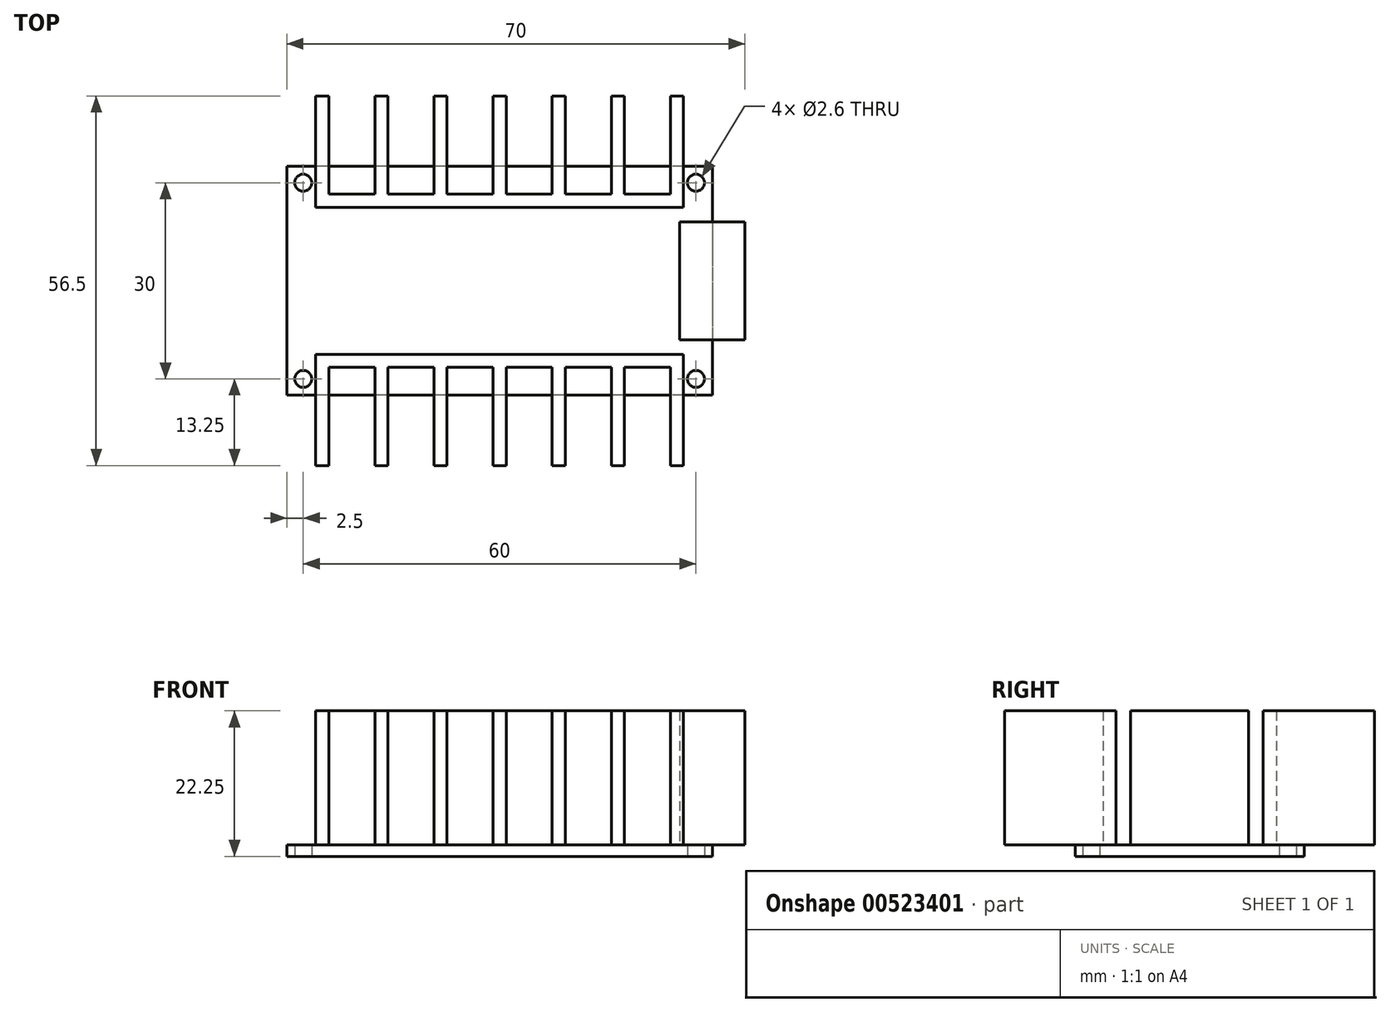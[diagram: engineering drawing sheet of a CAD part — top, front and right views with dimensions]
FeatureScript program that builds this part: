
annotation { "Feature Type Name" : "Feature", "Feature Type Description" : "" }
export const myFeature = defineFeature(function(context is Context, id is Id, definition is map)
    precondition{}
    {
        {
            var Q0;
            Q0=qCreatedBy(makeId("Top.planeOp"),FACE);
            var sketch = newSketch(context, id + "F0", { "sketchPlane" : qUnion([Q0])});
            skLineSegment(sketch, "E0.bottom", {"start": v(32.5, 17.5) * mm, "end": v(-32.5, 17.5) * mm});
            skLineSegment(sketch, "E0.top", {"start": v(32.5, -17.5) * mm, "end": v(-32.5, -17.5) * mm});
            skLineSegment(sketch, "E0.left", {"start": v(32.5, 17.5) * mm, "end": v(32.5, -17.5) * mm});
            skLineSegment(sketch, "E0.right", {"start": v(-32.5, 17.5) * mm, "end": v(-32.5, -17.5) * mm});
            skPoint(sketch, "E0.middle", {"position": v(0, 0) * mm});
            skCircle(sketch, "E1", {"center": v(-30, 15) * mm, "radius": 1.3 * mm});
            skCircle(sketch, "E2", {"center": v(30, 15) * mm, "radius": 1.3 * mm});
            skCircle(sketch, "E3", {"center": v(-30, -15) * mm, "radius": 1.3 * mm});
            skCircle(sketch, "E4", {"center": v(30, -15) * mm, "radius": 1.3 * mm});
            skLineSegment(sketch, "E5", {"start": v(-30, 15) * mm, "end": v(30, 15) * mm, "construction": true});
            skLineSegment(sketch, "E6", {"start": v(30, -15) * mm, "end": v(-30, -15) * mm, "construction": true});
            skLineSegment(sketch, "E7", {"start": v(-30, 15) * mm, "end": v(-30, -15) * mm, "construction": true});
            skLineSegment(sketch, "E8", {"start": v(30, 15) * mm, "end": v(30, -15) * mm, "construction": true});
            skLineSegment(sketch, "E9", {"start": v(0, -15) * mm, "end": v(0, -17.5) * mm, "construction": true});
            skLineSegment(sketch, "E10", {"start": v(0, 17.5) * mm, "end": v(0, 15) * mm, "construction": true});
            skLineSegment(sketch, "E11", {"start": v(-32.5, 0) * mm, "end": v(-30, 0) * mm, "construction": true});
            skLineSegment(sketch, "E12", {"start": v(30, 0) * mm, "end": v(32.5, 0) * mm, "construction": true});
            skSolve(sketch);
        }
        {
            var Q0;
            Q0 = qSketchRegion(id + "F0", true);
            extrude(context, id + "F1", {"entities" : qUnion([Q0]), "depth" : 1.75 * mm, "offsetDistance" : 25 * mm});
        }
        {
            var Q0;
            Q0=makeQuery(id+"F1.opExtrude","CAP_FACE",FACE,{"disambiguationData":[OSD([sQuery(id+"F0.wireOp",EDGE,"E0.bottom"),sQuery(id+"F0.wireOp",EDGE,"E0.top"),sQuery(id+"F0.wireOp",EDGE,"E0.left"),sQuery(id+"F0.wireOp",EDGE,"E0.right"),sQuery(id+"F0.wireOp",EDGE,"E1"),sQuery(id+"F0.wireOp",EDGE,"E2"),sQuery(id+"F0.wireOp",EDGE,"E3"),sQuery(id+"F0.wireOp",EDGE,"E4")])],"isStart":false});
            var sketch = newSketch(context, id + "F2", { "sketchPlane" : qUnion([Q0])});
            skLineSegment(sketch, "E13", {"start": v(-12.02, 0) * mm, "end": v(12.3, 0) * mm, "construction": true});
            skLineSegment(sketch, "E14.bottom", {"start": v(-28.1, 28.25) * mm, "end": v(-26.1, 28.25) * mm});
            skLineSegment(sketch, "E14.top", {"start": v(-28.1, 13.25) * mm, "end": v(-26.1, 13.25) * mm});
            skLineSegment(sketch, "E14.left", {"start": v(-28.1, 28.25) * mm, "end": v(-28.1, 13.25) * mm});
            skLineSegment(sketch, "E14.right", {"start": v(-26.1, 28.25) * mm, "end": v(-26.1, 13.25) * mm});
            skLineSegment(sketch, "E15.bottom", {"start": v(-10.03, 28.25) * mm, "end": v(-8.03, 28.25) * mm});
            skLineSegment(sketch, "E15.top", {"start": v(-10.03, 13.25) * mm, "end": v(-8.03, 13.25) * mm});
            skLineSegment(sketch, "E15.left", {"start": v(-10.03, 28.25) * mm, "end": v(-10.03, 13.25) * mm});
            skLineSegment(sketch, "E15.right", {"start": v(-8.03, 28.25) * mm, "end": v(-8.03, 13.25) * mm});
            skLineSegment(sketch, "E16.bottom", {"start": v(17.07, 28.25) * mm, "end": v(19.07, 28.25) * mm});
            skLineSegment(sketch, "E16.top", {"start": v(17.07, 13.25) * mm, "end": v(19.07, 13.25) * mm});
            skLineSegment(sketch, "E16.left", {"start": v(17.07, 28.25) * mm, "end": v(17.07, 13.25) * mm});
            skLineSegment(sketch, "E16.right", {"start": v(19.07, 28.25) * mm, "end": v(19.07, 13.25) * mm});
            skLineSegment(sketch, "E17.bottom", {"start": v(1, 28.25) * mm, "end": v(-1, 28.25) * mm});
            skLineSegment(sketch, "E17.top", {"start": v(1, 13.25) * mm, "end": v(-1, 13.25) * mm});
            skLineSegment(sketch, "E17.left", {"start": v(1, 28.25) * mm, "end": v(1, 13.25) * mm});
            skLineSegment(sketch, "E17.right", {"start": v(-1, 28.25) * mm, "end": v(-1, 13.25) * mm});
            skLineSegment(sketch, "E18.bottom", {"start": v(-19.07, 13.25) * mm, "end": v(-17.07, 13.25) * mm});
            skLineSegment(sketch, "E18.top", {"start": v(-19.07, 28.25) * mm, "end": v(-17.07, 28.25) * mm});
            skLineSegment(sketch, "E18.left", {"start": v(-19.07, 13.25) * mm, "end": v(-19.07, 28.25) * mm});
            skLineSegment(sketch, "E18.right", {"start": v(-17.07, 13.25) * mm, "end": v(-17.07, 28.25) * mm});
            skLineSegment(sketch, "E19.bottom", {"start": v(8.03, 13.25) * mm, "end": v(10.03, 13.25) * mm});
            skLineSegment(sketch, "E19.top", {"start": v(8.03, 28.25) * mm, "end": v(10.03, 28.25) * mm});
            skLineSegment(sketch, "E19.left", {"start": v(8.03, 13.25) * mm, "end": v(8.03, 28.25) * mm});
            skLineSegment(sketch, "E19.right", {"start": v(10.03, 13.25) * mm, "end": v(10.03, 28.25) * mm});
            skLineSegment(sketch, "E20.bottom", {"start": v(26.1, 28.25) * mm, "end": v(28.1, 28.25) * mm});
            skLineSegment(sketch, "E20.top", {"start": v(26.1, 13.25) * mm, "end": v(28.1, 13.25) * mm});
            skLineSegment(sketch, "E20.left", {"start": v(26.1, 28.25) * mm, "end": v(26.1, 13.25) * mm});
            skLineSegment(sketch, "E20.right", {"start": v(28.1, 28.25) * mm, "end": v(28.1, 13.25) * mm});
            skLineSegment(sketch, "E21.bottom", {"start": v(-28.1, 13.25) * mm, "end": v(28.1, 13.25) * mm});
            skLineSegment(sketch, "E21.top", {"start": v(-28.1, 11.25) * mm, "end": v(28.1, 11.25) * mm});
            skLineSegment(sketch, "E21.left", {"start": v(-28.1, 13.25) * mm, "end": v(-28.1, 11.25) * mm});
            skLineSegment(sketch, "E21.right", {"start": v(28.1, 13.25) * mm, "end": v(28.1, 11.25) * mm});
            skPoint(sketch, "E22", {"position": v(0, 11.25) * mm});
            skLineSegment(sketch, "E23", {"start": v(-26.1, 28.25) * mm, "end": v(-19.07, 28.25) * mm, "construction": true});
            skLineSegment(sketch, "E24", {"start": v(-17.07, 28.25) * mm, "end": v(-10.03, 28.25) * mm, "construction": true});
            skLineSegment(sketch, "E25", {"start": v(-8.03, 28.25) * mm, "end": v(-1, 28.25) * mm, "construction": true});
            skLineSegment(sketch, "E26", {"start": v(1, 28.25) * mm, "end": v(8.03, 28.25) * mm, "construction": true});
            skLineSegment(sketch, "E27", {"start": v(10.03, 28.25) * mm, "end": v(17.07, 28.25) * mm, "construction": true});
            skLineSegment(sketch, "E28", {"start": v(19.07, 28.25) * mm, "end": v(26.1, 28.25) * mm, "construction": true});
            skLineSegment(sketch, "E29.MirrorCS", {"start": v(-10.03, -28.25) * mm, "end": v(-10.03, -13.25) * mm});
            skLineSegment(sketch, "E30.MirrorCS", {"start": v(-19.07, -13.25) * mm, "end": v(-19.07, -28.25) * mm});
            skLineSegment(sketch, "E31.MirrorCS", {"start": v(28.1, -13.25) * mm, "end": v(28.1, -11.25) * mm});
            skLineSegment(sketch, "E32.MirrorCS", {"start": v(10.03, -28.25) * mm, "end": v(17.07, -28.25) * mm, "construction": true});
            skLineSegment(sketch, "E33.MirrorCS", {"start": v(-8.03, -28.25) * mm, "end": v(-1, -28.25) * mm, "construction": true});
            skLineSegment(sketch, "E34.MirrorCS", {"start": v(-1, -28.25) * mm, "end": v(-1, -13.25) * mm});
            skLineSegment(sketch, "E35.MirrorCS", {"start": v(26.1, -28.25) * mm, "end": v(26.1, -13.25) * mm});
            skLineSegment(sketch, "E36.MirrorCS", {"start": v(-26.1, -28.25) * mm, "end": v(-26.1, -13.25) * mm});
            skLineSegment(sketch, "E37.MirrorCS", {"start": v(1, -13.25) * mm, "end": v(-1, -13.25) * mm});
            skLineSegment(sketch, "E38.MirrorCS", {"start": v(17.07, -28.25) * mm, "end": v(19.07, -28.25) * mm});
            skLineSegment(sketch, "E39.MirrorCS", {"start": v(-17.07, -13.25) * mm, "end": v(-17.07, -28.25) * mm});
            skLineSegment(sketch, "E40.MirrorCS", {"start": v(-26.1, -28.25) * mm, "end": v(-19.07, -28.25) * mm, "construction": true});
            skLineSegment(sketch, "E41.MirrorCS", {"start": v(-10.03, -13.25) * mm, "end": v(-8.03, -13.25) * mm});
            skLineSegment(sketch, "E42.MirrorCS", {"start": v(-28.1, -13.25) * mm, "end": v(-26.1, -13.25) * mm});
            skLineSegment(sketch, "E43.MirrorCS", {"start": v(26.1, -13.25) * mm, "end": v(28.1, -13.25) * mm});
            skLineSegment(sketch, "E44.MirrorCS", {"start": v(-28.1, -11.25) * mm, "end": v(28.1, -11.25) * mm});
            skLineSegment(sketch, "E45.MirrorCS", {"start": v(-28.1, -28.25) * mm, "end": v(-26.1, -28.25) * mm});
            skLineSegment(sketch, "E46.MirrorCS", {"start": v(1, -28.25) * mm, "end": v(1, -13.25) * mm});
            skLineSegment(sketch, "E47.MirrorCS", {"start": v(8.03, -13.25) * mm, "end": v(10.03, -13.25) * mm});
            skLineSegment(sketch, "E48.MirrorCS", {"start": v(17.07, -13.25) * mm, "end": v(19.07, -13.25) * mm});
            skLineSegment(sketch, "E49.MirrorCS", {"start": v(-8.03, -28.25) * mm, "end": v(-8.03, -13.25) * mm});
            skLineSegment(sketch, "E50.MirrorCS", {"start": v(-28.1, -13.25) * mm, "end": v(28.1, -13.25) * mm});
            skLineSegment(sketch, "E51.MirrorCS", {"start": v(1, -28.25) * mm, "end": v(8.03, -28.25) * mm, "construction": true});
            skLineSegment(sketch, "E52.MirrorCS", {"start": v(8.03, -28.25) * mm, "end": v(10.03, -28.25) * mm});
            skLineSegment(sketch, "E53.MirrorCS", {"start": v(-28.1, -13.25) * mm, "end": v(-28.1, -11.25) * mm});
            skLineSegment(sketch, "E54.MirrorCS", {"start": v(-19.07, -28.25) * mm, "end": v(-17.07, -28.25) * mm});
            skLineSegment(sketch, "E55.MirrorCS", {"start": v(-17.07, -28.25) * mm, "end": v(-10.03, -28.25) * mm, "construction": true});
            skLineSegment(sketch, "E56.MirrorCS", {"start": v(-10.03, -28.25) * mm, "end": v(-8.03, -28.25) * mm});
            skLineSegment(sketch, "E57.MirrorCS", {"start": v(1, -28.25) * mm, "end": v(-1, -28.25) * mm});
            skPoint(sketch, "E58.MirrorP", {"position": v(0, -11.25) * mm});
            skLineSegment(sketch, "E59.MirrorCS", {"start": v(19.07, -28.25) * mm, "end": v(26.1, -28.25) * mm, "construction": true});
            skLineSegment(sketch, "E60.MirrorCS", {"start": v(19.07, -28.25) * mm, "end": v(19.07, -13.25) * mm});
            skLineSegment(sketch, "E61.MirrorCS", {"start": v(26.1, -28.25) * mm, "end": v(28.1, -28.25) * mm});
            skLineSegment(sketch, "E62.MirrorCS", {"start": v(8.03, -13.25) * mm, "end": v(8.03, -28.25) * mm});
            skLineSegment(sketch, "E63.MirrorCS", {"start": v(17.07, -28.25) * mm, "end": v(17.07, -13.25) * mm});
            skLineSegment(sketch, "E64.MirrorCS", {"start": v(28.1, -28.25) * mm, "end": v(28.1, -13.25) * mm});
            skLineSegment(sketch, "E65.MirrorCS", {"start": v(10.03, -13.25) * mm, "end": v(10.03, -28.25) * mm});
            skLineSegment(sketch, "E66.MirrorCS", {"start": v(-19.07, -13.25) * mm, "end": v(-17.07, -13.25) * mm});
            skLineSegment(sketch, "E67.MirrorCS", {"start": v(-28.1, -28.25) * mm, "end": v(-28.1, -13.25) * mm});
            skSolve(sketch);
        }
        {
            var Q0;
            Q0 = qSketchRegion(id + "F2", true);
            extrude(context, id + "F3", {"entities" : qUnion([Q0]), "operationType" : NewBodyOperationType.ADD, "depth" : 20.5 * mm, "offsetDistance" : 25 * mm});
        }
        {
            var Q0;
            {var subQ5=sQuery(id+"F0.wireOp",EDGE,"E0.right");var subQ6=sQuery(id+"F0.wireOp",EDGE,"E4");var subQ9=sQuery(id+"F0.wireOp",EDGE,"E3");var subQ10=sQuery(id+"F0.wireOp",EDGE,"E2");var subQ11=sQuery(id+"F0.wireOp",EDGE,"E1");var subQ12=sQuery(id+"F0.wireOp",EDGE,"E0.bottom");var subQ13=sQuery(id+"F0.wireOp",EDGE,"E0.top");var subQ14=sQuery(id+"F0.wireOp",EDGE,"E0.left");Q0=makeQuery(id+"F3.boolean.opBoolean","SPLIT",FACE,{"disambiguationData":[TD([makeQuery(id+"F1.opExtrude","SWEPT_FACE",FACE,{"disambiguationData":[OSD([subQ14])]})])],"derivedFrom":makeQuery(id+"F1.opExtrude","CAP_FACE",FACE,{"disambiguationData":[OSD([subQ12,subQ13,subQ14,subQ5,subQ11,subQ10,subQ9,subQ6])],"isStart":false})});}
            var sketch = newSketch(context, id + "F4", { "sketchPlane" : qUnion([Q0])});
            skLineSegment(sketch, "E68.bottom", {"start": v(37.5, 9) * mm, "end": v(27.5, 9) * mm});
            skLineSegment(sketch, "E68.top", {"start": v(37.5, -9) * mm, "end": v(27.5, -9) * mm});
            skLineSegment(sketch, "E68.left", {"start": v(37.5, 9) * mm, "end": v(37.5, -9) * mm});
            skLineSegment(sketch, "E68.right", {"start": v(27.5, 9) * mm, "end": v(27.5, -9) * mm});
            skPoint(sketch, "E68.middle", {"position": v(32.5, 0) * mm});
            skSolve(sketch);
        }
        {
            var Q0;
            Q0 = qSketchRegion(id + "F4", true);
            var Q1;
            Q1=makeQuery(id+"F3.opExtrude","CAP_FACE",FACE,{"disambiguationData":[OSD([sQuery(id+"F2.wireOp",EDGE,"E14.bottom"),sQuery(id+"F2.wireOp",EDGE,"E14.left"),sQuery(id+"F2.wireOp",EDGE,"E14.right"),sQuery(id+"F2.wireOp",EDGE,"E15.bottom"),sQuery(id+"F2.wireOp",EDGE,"E15.left"),sQuery(id+"F2.wireOp",EDGE,"E15.right"),sQuery(id+"F2.wireOp",EDGE,"E16.bottom"),sQuery(id+"F2.wireOp",EDGE,"E16.left"),sQuery(id+"F2.wireOp",EDGE,"E16.right"),sQuery(id+"F2.wireOp",EDGE,"E17.bottom"),sQuery(id+"F2.wireOp",EDGE,"E17.left"),sQuery(id+"F2.wireOp",EDGE,"E17.right"),sQuery(id+"F2.wireOp",EDGE,"E18.top"),sQuery(id+"F2.wireOp",EDGE,"E18.left"),sQuery(id+"F2.wireOp",EDGE,"E18.right"),sQuery(id+"F2.wireOp",EDGE,"E19.top"),sQuery(id+"F2.wireOp",EDGE,"E19.left"),sQuery(id+"F2.wireOp",EDGE,"E19.right"),sQuery(id+"F2.wireOp",EDGE,"E20.bottom"),sQuery(id+"F2.wireOp",EDGE,"E20.left"),sQuery(id+"F2.wireOp",EDGE,"E20.right"),sQuery(id+"F2.wireOp",EDGE,"E21.bottom"),sQuery(id+"F2.wireOp",EDGE,"E21.top"),sQuery(id+"F2.wireOp",EDGE,"E21.left"),sQuery(id+"F2.wireOp",EDGE,"E21.right")])],"isStart":false});
            extrude(context, id + "F5", {"entities" : qUnion([Q0]), "operationType" : NewBodyOperationType.ADD, "endBound" : BoundingType.UP_TO_SURFACE, "depth" : 25 * mm, "endBoundEntityFace" : qUnion([Q1]), "offsetDistance" : 25 * mm});
        }
    });
